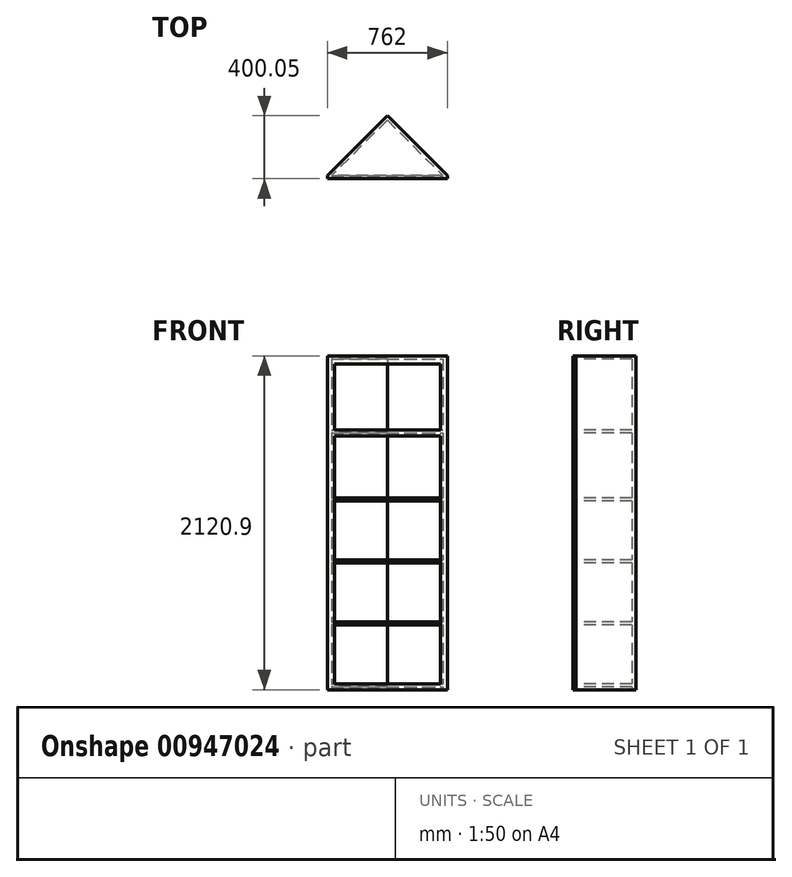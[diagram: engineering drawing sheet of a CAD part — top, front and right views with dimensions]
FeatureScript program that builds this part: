
annotation { "Feature Type Name" : "Feature", "Feature Type Description" : "" }
export const myFeature = defineFeature(function(context is Context, id is Id, definition is map)
    precondition{}
    {
        {
            var Q0;
            Q0=qCreatedBy(makeId("Top.planeOp"),FACE);
            var sketch = newSketch(context, id + "F0", { "sketchPlane" : qUnion([Q0])});
            skLineSegment(sketch, "E0", {"start": v(-381, -381) * mm, "end": v(381, -381) * mm});
            skLineSegment(sketch, "E1", {"start": v(381, -381) * mm, "end": v(0, 0) * mm});
            skLineSegment(sketch, "E2", {"start": v(0, 0) * mm, "end": v(-381, -381) * mm});
            skLineSegment(sketch, "E3", {"start": v(-381, -381) * mm, "end": v(-381, -400.05) * mm});
            skLineSegment(sketch, "E4", {"start": v(-381, -400.05) * mm, "end": v(381, -400.05) * mm});
            skLineSegment(sketch, "E5", {"start": v(381, -400.05) * mm, "end": v(381, -381) * mm});
            skLineSegment(sketch, "E6", {"start": v(0, 0) * mm, "end": v(0, -26.94) * mm});
            skLineSegment(sketch, "E7", {"start": v(0, -26.94) * mm, "end": v(-354.06, -381) * mm});
            skLineSegment(sketch, "E8", {"start": v(0, -26.94) * mm, "end": v(354.06, -381) * mm});
            skSolve(sketch);
        }
        {
            var Q0;
            Q0=makeQuery(id+"F0.imprint","IMPRINT",FACE,{"disambiguationData":[TD([[makeQuery(id+"F0.imprint","IMPRINT",EDGE,{"derivedFrom":sQuery(id+"F0.wireOp",EDGE,"E0")}),-1.0]])]});
            extrude(context, id + "F1", {"entities" : qUnion([Q0]), "depth" : 2133.6 * mm, "offsetDistance" : 25.4 * mm});
        }
        {
            var Q0;
            {var subQ0=sQuery(id+"F0.wireOp",EDGE,"E1");Q0=makeQuery(id+"F0.imprint","IMPRINT",FACE,{"disambiguationData":[TD([[makeQuery(id+"F0.imprint","IMPRINT",EDGE,{"derivedFrom":subQ0}),1.0]])]});}
            var Q1;
            {var subQ0=sQuery(id+"F0.wireOp",EDGE,"E2");Q1=makeQuery(id+"F0.imprint","IMPRINT",FACE,{"disambiguationData":[TD([[makeQuery(id+"F0.imprint","IMPRINT",EDGE,{"derivedFrom":subQ0}),1.0]])]});}
            extrude(context, id + "F2", {"entities" : qUnion([Q0, Q1]), "operationType" : NewBodyOperationType.ADD, "depth" : 2133.6 * mm, "offsetDistance" : 25.4 * mm});
        }
        {
            var Q0;
            {var subQ0=sQuery(id+"F0.wireOp",EDGE,"E7");Q0=makeQuery(id+"F0.imprint","IMPRINT",FACE,{"disambiguationData":[TD([[makeQuery(id+"F0.imprint","IMPRINT",EDGE,{"derivedFrom":subQ0}),1.0]])]});}
            extrude(context, id + "F3", {"entities" : qUnion([Q0]), "operationType" : NewBodyOperationType.ADD, "depth" : 2133.6 * mm, "offsetDistance" : 25.4 * mm});
        }
        {
            var Q0;
            {var subQ0=sQuery(id+"F0.wireOp",EDGE,"E7");Q0=makeQuery(id+"F0.imprint","IMPRINT",FACE,{"disambiguationData":[TD([[makeQuery(id+"F0.imprint","IMPRINT",EDGE,{"derivedFrom":subQ0}),1.0]])]});}
            extrude(context, id + "F4", {"entities" : qUnion([Q0]), "operationType" : NewBodyOperationType.REMOVE, "depth" : 1905 * mm, "offsetDistance" : 25.4 * mm});
        }
        {
            var Q0;
            Q0=makeQuery(id+"F1.opExtrude","SWEPT_FACE",FACE,{"disambiguationData":[OSD([sQuery(id+"F0.wireOp",EDGE,"E4")])]});
            var sketch = newSketch(context, id + "F5", { "sketchPlane" : qUnion([Q0])});
            skLineSegment(sketch, "E9.bottom", {"start": v(381, 2133.6) * mm, "end": v(-381, 2133.6) * mm});
            skLineSegment(sketch, "E9.top", {"start": v(381, 0) * mm, "end": v(-381, 0) * mm});
            skLineSegment(sketch, "E9.left", {"start": v(381, 2133.6) * mm, "end": v(381, 0) * mm});
            skLineSegment(sketch, "E9.right", {"start": v(-381, 2133.6) * mm, "end": v(-381, 0) * mm});
            skLineSegment(sketch, "E10", {"start": v(-336.55, 2133.6) * mm, "end": v(-336.55, 12.7) * mm});
            skLineSegment(sketch, "E11", {"start": v(336.55, 2133.6) * mm, "end": v(336.55, 12.7) * mm});
            skLineSegment(sketch, "E12", {"start": v(336.55, 1663.7) * mm, "end": v(-336.55, 1663.7) * mm});
            skLineSegment(sketch, "E13", {"start": v(-336.55, 1625.6) * mm, "end": v(336.55, 1625.6) * mm});
            skLineSegment(sketch, "E14", {"start": v(336.55, 2082.8) * mm, "end": v(-336.55, 2082.8) * mm});
            skLineSegment(sketch, "E15", {"start": v(-336.55, 50.8) * mm, "end": v(336.55, 50.8) * mm});
            skLineSegment(sketch, "E16", {"start": v(336.55, 12.7) * mm, "end": v(-336.55, 12.7) * mm});
            skLineSegment(sketch, "E17", {"start": v(-336.55, 12.7) * mm, "end": v(-381, 12.7) * mm});
            skLineSegment(sketch, "E18", {"start": v(336.55, 12.7) * mm, "end": v(381, 12.7) * mm});
            skSolve(sketch);
        }
        {
            var Q0;
            {var subQ0=sQuery(id+"F5.wireOp",EDGE,"E12");Q0=makeQuery(id+"F5.imprint","IMPRINT",FACE,{"disambiguationData":[TD([[makeQuery(id+"F5.imprint","IMPRINT",EDGE,{"derivedFrom":subQ0}),-1.0]])]});}
            var Q1;
            {var subQ0=sQuery(id+"F5.wireOp",EDGE,"E13");Q1=makeQuery(id+"F5.imprint","IMPRINT",FACE,{"disambiguationData":[TD([[makeQuery(id+"F5.imprint","IMPRINT",EDGE,{"derivedFrom":subQ0}),-1.0]])]});}
            extrude(context, id + "F6", {"entities" : qUnion([Q0, Q1]), "operationType" : NewBodyOperationType.REMOVE, "oppositeDirection" : true, "depth" : 19.05 * mm, "offsetDistance" : 25.4 * mm});
        }
        {
            var Q0;
            Q0=makeQuery(id+"F4.boolean.opBoolean","COPY",FACE,{"derivedFrom":makeQuery(id+"F4.opExtrude","CAP_FACE",FACE,{"disambiguationData":[OSD([sQuery(id+"F0.wireOp",EDGE,"E0"),sQuery(id+"F0.wireOp",EDGE,"E7"),sQuery(id+"F0.wireOp",EDGE,"E8")])],"isStart":false})});
            extrude(context, id + "F7", {"entities" : qUnion([Q0]), "operationType" : NewBodyOperationType.REMOVE, "oppositeDirection" : true, "depth" : 209.55 * mm, "offsetDistance" : 25.4 * mm});
        }
        {
            var Q0;
            {var subQ0=sQuery(id+"F0.wireOp",EDGE,"E7");Q0=makeQuery(id+"F0.imprint","IMPRINT",FACE,{"disambiguationData":[TD([[makeQuery(id+"F0.imprint","IMPRINT",EDGE,{"derivedFrom":subQ0}),1.0]])]});}
            var Q1;
            Q1=makeQuery(id+"F6.boolean.opBoolean","COPY",FACE,{"derivedFrom":makeQuery(id+"F6.opExtrude","SWEPT_FACE",FACE,{"disambiguationData":[OSD([sQuery(id+"F5.wireOp",EDGE,"E12")])]})});
            extrude(context, id + "F8", {"entities" : qUnion([Q0]), "operationType" : NewBodyOperationType.ADD, "depth" : 1663.7 * mm, "endBoundEntityFace" : qUnion([Q1]), "offsetDistance" : 25.4 * mm});
        }
        {
            var Q0;
            {var subQ0=sQuery(id+"F0.wireOp",EDGE,"E7");Q0=makeQuery(id+"F0.imprint","IMPRINT",FACE,{"disambiguationData":[TD([[makeQuery(id+"F0.imprint","IMPRINT",EDGE,{"derivedFrom":subQ0}),1.0]])]});}
            extrude(context, id + "F9", {"entities" : qUnion([Q0]), "operationType" : NewBodyOperationType.REMOVE, "depth" : 1644.65 * mm, "offsetDistance" : 25.4 * mm});
        }
        {
            var Q0;
            {var subQ0=sQuery(id+"F0.wireOp",EDGE,"E7");Q0=makeQuery(id+"F0.imprint","IMPRINT",FACE,{"disambiguationData":[TD([[makeQuery(id+"F0.imprint","IMPRINT",EDGE,{"derivedFrom":subQ0}),1.0]])]});}
            extrude(context, id + "F10", {"entities" : qUnion([Q0]), "operationType" : NewBodyOperationType.ADD, "depth" : 1231.9 * mm, "offsetDistance" : 25.4 * mm});
        }
        {
            var Q0;
            {var subQ0=sQuery(id+"F0.wireOp",EDGE,"E7");Q0=makeQuery(id+"F0.imprint","IMPRINT",FACE,{"disambiguationData":[TD([[makeQuery(id+"F0.imprint","IMPRINT",EDGE,{"derivedFrom":subQ0}),1.0]])]});}
            extrude(context, id + "F11", {"entities" : qUnion([Q0]), "operationType" : NewBodyOperationType.REMOVE, "depth" : 1212.85 * mm, "offsetDistance" : 25.4 * mm});
        }
        {
            var Q0;
            {var subQ0=sQuery(id+"F0.wireOp",EDGE,"E7");Q0=makeQuery(id+"F0.imprint","IMPRINT",FACE,{"disambiguationData":[TD([[makeQuery(id+"F0.imprint","IMPRINT",EDGE,{"derivedFrom":subQ0}),1.0]])]});}
            extrude(context, id + "F12", {"entities" : qUnion([Q0]), "operationType" : NewBodyOperationType.ADD, "depth" : 787.4 * mm, "offsetDistance" : 25.4 * mm});
        }
        {
            var Q0;
            {var subQ0=sQuery(id+"F0.wireOp",EDGE,"E7");Q0=makeQuery(id+"F0.imprint","IMPRINT",FACE,{"disambiguationData":[TD([[makeQuery(id+"F0.imprint","IMPRINT",EDGE,{"derivedFrom":subQ0}),1.0]])]});}
            extrude(context, id + "F13", {"entities" : qUnion([Q0]), "operationType" : NewBodyOperationType.REMOVE, "depth" : 768.35 * mm, "offsetDistance" : 25.4 * mm});
        }
        {
            var Q0;
            {var subQ0=sQuery(id+"F0.wireOp",EDGE,"E7");Q0=makeQuery(id+"F0.imprint","IMPRINT",FACE,{"disambiguationData":[TD([[makeQuery(id+"F0.imprint","IMPRINT",EDGE,{"derivedFrom":subQ0}),1.0]])]});}
            extrude(context, id + "F14", {"entities" : qUnion([Q0]), "operationType" : NewBodyOperationType.ADD, "depth" : 393.7 * mm, "offsetDistance" : 25.4 * mm});
        }
        {
            var Q0;
            {var subQ0=sQuery(id+"F0.wireOp",EDGE,"E7");Q0=makeQuery(id+"F0.imprint","IMPRINT",FACE,{"disambiguationData":[TD([[makeQuery(id+"F0.imprint","IMPRINT",EDGE,{"derivedFrom":subQ0}),1.0]])]});}
            extrude(context, id + "F15", {"entities" : qUnion([Q0]), "operationType" : NewBodyOperationType.REMOVE, "depth" : 374.65 * mm, "offsetDistance" : 25.4 * mm});
        }
        {
            var Q0;
            {var subQ0=sQuery(id+"F0.wireOp",EDGE,"E7");Q0=makeQuery(id+"F0.imprint","IMPRINT",FACE,{"disambiguationData":[TD([[makeQuery(id+"F0.imprint","IMPRINT",EDGE,{"derivedFrom":subQ0}),1.0]])]});}
            extrude(context, id + "F16", {"entities" : qUnion([Q0]), "operationType" : NewBodyOperationType.ADD, "depth" : 50.8 * mm, "offsetDistance" : 25.4 * mm});
        }
        {
            var Q0;
            {var subQ0=sQuery(id+"F0.wireOp",EDGE,"E7");Q0=makeQuery(id+"F0.imprint","IMPRINT",FACE,{"disambiguationData":[TD([[makeQuery(id+"F0.imprint","IMPRINT",EDGE,{"derivedFrom":subQ0}),1.0]])]});}
            extrude(context, id + "F17", {"entities" : qUnion([Q0]), "operationType" : NewBodyOperationType.REMOVE, "depth" : 31.75 * mm, "offsetDistance" : 25.4 * mm});
        }
        {
            var Q0;
            Q0=makeQuery(id+"F12.opExtrude","CAP_FACE",FACE,{"disambiguationData":[OSD([sQuery(id+"F0.wireOp",EDGE,"E0"),sQuery(id+"F0.wireOp",EDGE,"E7"),sQuery(id+"F0.wireOp",EDGE,"E8")])],"isStart":false});
            extrude(context, id + "F18", {"entities" : qUnion([Q0]), "operationType" : NewBodyOperationType.ADD, "depth" : 50.8 * mm, "offsetDistance" : 25.4 * mm});
        }
        {
            var Q0;
            Q0=makeQuery(id+"F13.boolean.opBoolean","COPY",FACE,{"derivedFrom":makeQuery(id+"F13.opExtrude","CAP_FACE",FACE,{"disambiguationData":[OSD([sQuery(id+"F0.wireOp",EDGE,"E0"),sQuery(id+"F0.wireOp",EDGE,"E7"),sQuery(id+"F0.wireOp",EDGE,"E8")])],"isStart":false})});
            extrude(context, id + "F19", {"entities" : qUnion([Q0]), "operationType" : NewBodyOperationType.REMOVE, "oppositeDirection" : true, "depth" : 50.8 * mm, "offsetDistance" : 25.4 * mm});
        }
        {
            var Q0;
            Q0=makeQuery(id+"F14.opExtrude","CAP_FACE",FACE,{"disambiguationData":[OSD([sQuery(id+"F0.wireOp",EDGE,"E0"),sQuery(id+"F0.wireOp",EDGE,"E7"),sQuery(id+"F0.wireOp",EDGE,"E8")])],"isStart":false});
            extrude(context, id + "F20", {"entities" : qUnion([Q0]), "operationType" : NewBodyOperationType.ADD, "depth" : 50.8 * mm, "offsetDistance" : 25.4 * mm});
        }
        {
            var Q0;
            Q0=makeQuery(id+"F15.boolean.opBoolean","COPY",FACE,{"derivedFrom":makeQuery(id+"F15.opExtrude","CAP_FACE",FACE,{"disambiguationData":[OSD([sQuery(id+"F0.wireOp",EDGE,"E0"),sQuery(id+"F0.wireOp",EDGE,"E7"),sQuery(id+"F0.wireOp",EDGE,"E8")])],"isStart":false})});
            extrude(context, id + "F21", {"entities" : qUnion([Q0]), "operationType" : NewBodyOperationType.REMOVE, "oppositeDirection" : true, "depth" : 50.8 * mm, "offsetDistance" : 25.4 * mm});
        }
        {
            var Q0;
            {var subQ0=sQuery(id+"F0.wireOp",EDGE,"E1");Q0=makeQuery(id+"F0.imprint","IMPRINT",FACE,{"disambiguationData":[TD([[makeQuery(id+"F0.imprint","IMPRINT",EDGE,{"derivedFrom":subQ0}),1.0]])]});}
            var Q1;
            {var subQ0=sQuery(id+"F0.wireOp",EDGE,"E2");Q1=makeQuery(id+"F0.imprint","IMPRINT",FACE,{"disambiguationData":[TD([[makeQuery(id+"F0.imprint","IMPRINT",EDGE,{"derivedFrom":subQ0}),1.0]])]});}
            var Q2;
            {var subQ4=sQuery(id+"F0.wireOp",EDGE,"E3");Q2=makeQuery(id+"F0.imprint","IMPRINT",FACE,{"disambiguationData":[TD([[makeQuery(id+"F0.imprint","IMPRINT",EDGE,{"derivedFrom":subQ4}),1.0]])]});}
            extrude(context, id + "F22", {"entities" : qUnion([Q0, Q1, Q2]), "operationType" : NewBodyOperationType.REMOVE, "depth" : 12.7 * mm, "offsetDistance" : 25.4 * mm});
        }
    });
